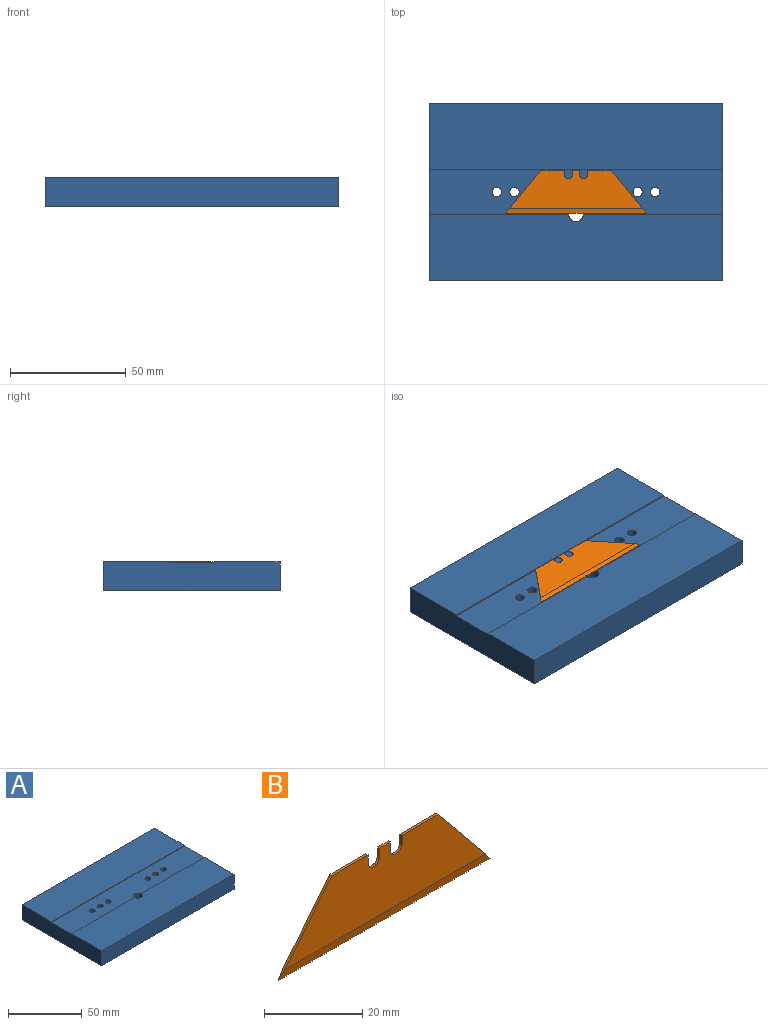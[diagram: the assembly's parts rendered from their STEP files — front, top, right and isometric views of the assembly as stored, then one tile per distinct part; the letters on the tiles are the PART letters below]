
ASSEMBLY  parts=2 mates=1
PART A: 18 faces, bbox 127x76.2x12.7 mm
  f0: plane 127x28.45mm, normal (0,0,1), area 3597.1mm2, adj f1,f2,f4,f5,f7,f11
  f1: plane 60.33x0.33mm, normal (0,1,0), area 19.9mm2, adj f0,f7,f10,f11
  f2: plane 60.33x0.33mm, normal (0,1,0), area 19.9mm2, adj f0,f5,f10,f11
  f3: plane 127x28.45mm, normal (0,0,1), area 3612.9mm2, adj f5,f6,f7,f9
  f4: plane 127x12.45mm, normal (0,-1,0), area 1580.6mm2, adj f0,f5,f7,f8
  f5: plane 76.2x12.7mm, normal (1,0,0), area 949.2mm2, adj f0,f2,f3,f4,f6,f8,f9,f10
  f6: plane 127x12.7mm, normal (0,1,0), area 1612.9mm2, adj f3,f5,f7,f8
  f7: plane 76.2x12.7mm, normal (-1,0,0), area 949.2mm2, adj f0,f1,f3,f4,f6,f8,f9,f10
  f8: plane 127x76.2mm, normal (0,0,-1), area 9568.9mm2, adj f4,f5,f6,f7,f11,f12,f13,f14
  f9: plane 127x0.58mm, normal (0,-1,0), area 74.2mm2, adj f3,f5,f7,f10
  f10: plane 127x19.3mm, normal (0,0,1), area 2358.9mm2, adj f1,f2,f5,f7,f9,f11,f12,f13
  f11: cylinder r=3.17mm len=12.45mm, axis (0,0,1), area 245mm2, adj f0,f1,f2,f8,f10
  f12: cylinder r=2.02mm len=12.12mm, axis (0,0,1), area 153.7mm2, adj f8,f10
  f13: cylinder r=2.02mm len=12.12mm, axis (0,0,1), area 153.7mm2, adj f8,f10
  f14: cylinder r=2.02mm len=12.12mm, axis (0,0,1), area 153.7mm2, adj f8,f10
  f15: cylinder r=2.02mm len=12.12mm, axis (0,0,1), area 153.7mm2, adj f8,f10
  f16: cylinder r=2.02mm len=12.12mm, axis (0,0,1), area 153.7mm2, adj f8,f10
  f17: cylinder r=2.02mm len=12.12mm, axis (0,0,1), area 153.7mm2, adj f8,f10
PART B: 15 faces, bbox 61x0.6x18.7 mm
  f0: plane 61x2.08mm, normal (0,0.99,-0.14), area 124.6mm2, adj f1,f2,f9,f11
  f1: plane 61x2.08mm, normal (0,-0.99,-0.14), area 124.6mm2, adj f0,f2,f9,f13
  f2: plane 18.7x15.25mm, normal (0.77,0,0.63), area 13.7mm2, adj f0,f1,f3,f11,f13
  f3: plane 10.35x0.6mm, normal (0,0,1), area 6.2mm2, adj f2,f4,f11,f13
  f4: plane 2.08x0.6mm, normal (-1,0,0), area 1.2mm2, adj f3,f5,f11,f13
  f5: cylinder r=1.68mm len=3.35mm, axis (0,-1,0), area 3.2mm2, adj f4,f6,f11,f13
  f6: plane 2.08x0.6mm, normal (1,0,0), area 1.2mm2, adj f5,f7,f11,f13
  f7: plane 3.1x0.6mm, normal (0,0,1), area 1.9mm2, adj f6,f8,f11,f13
  f8: plane 2.08x0.6mm, normal (-1,0,0), area 1.2mm2, adj f7,f10,f11,f13
  f9: plane 18.7x15.25mm, normal (-0.77,0,0.63), area 13.7mm2, adj f0,f1,f11,f12,f13
  f10: cylinder r=1.68mm len=3.35mm, axis (0,-1,0), area 3.2mm2, adj f8,f11,f13,f14
  f11: plane 57.61x16.62mm, normal (0,1,0), area 709.5mm2, adj f0,f2,f3,f4,f5,f6,f7,f8
  f12: plane 10.35x0.6mm, normal (0,0,1), area 6.2mm2, adj f9,f11,f13,f14
  f13: plane 57.61x16.62mm, normal (0,-1,0), area 709.5mm2, adj f1,f2,f3,f4,f5,f6,f7,f8
  f14: plane 2.08x0.6mm, normal (1,0,0), area 1.2mm2, adj f10,f11,f12,f13
PLACE A t=(24.07,19.2,-12.26)mm fixed
PLACE B rot(axis=(-1,0,0),90deg) t=(98.33,9.96,-0.14)mm
MATE fastened A.f10 <-> B.f11  axis (0,0,1) through (24.07,19.26,-0.14)mm
